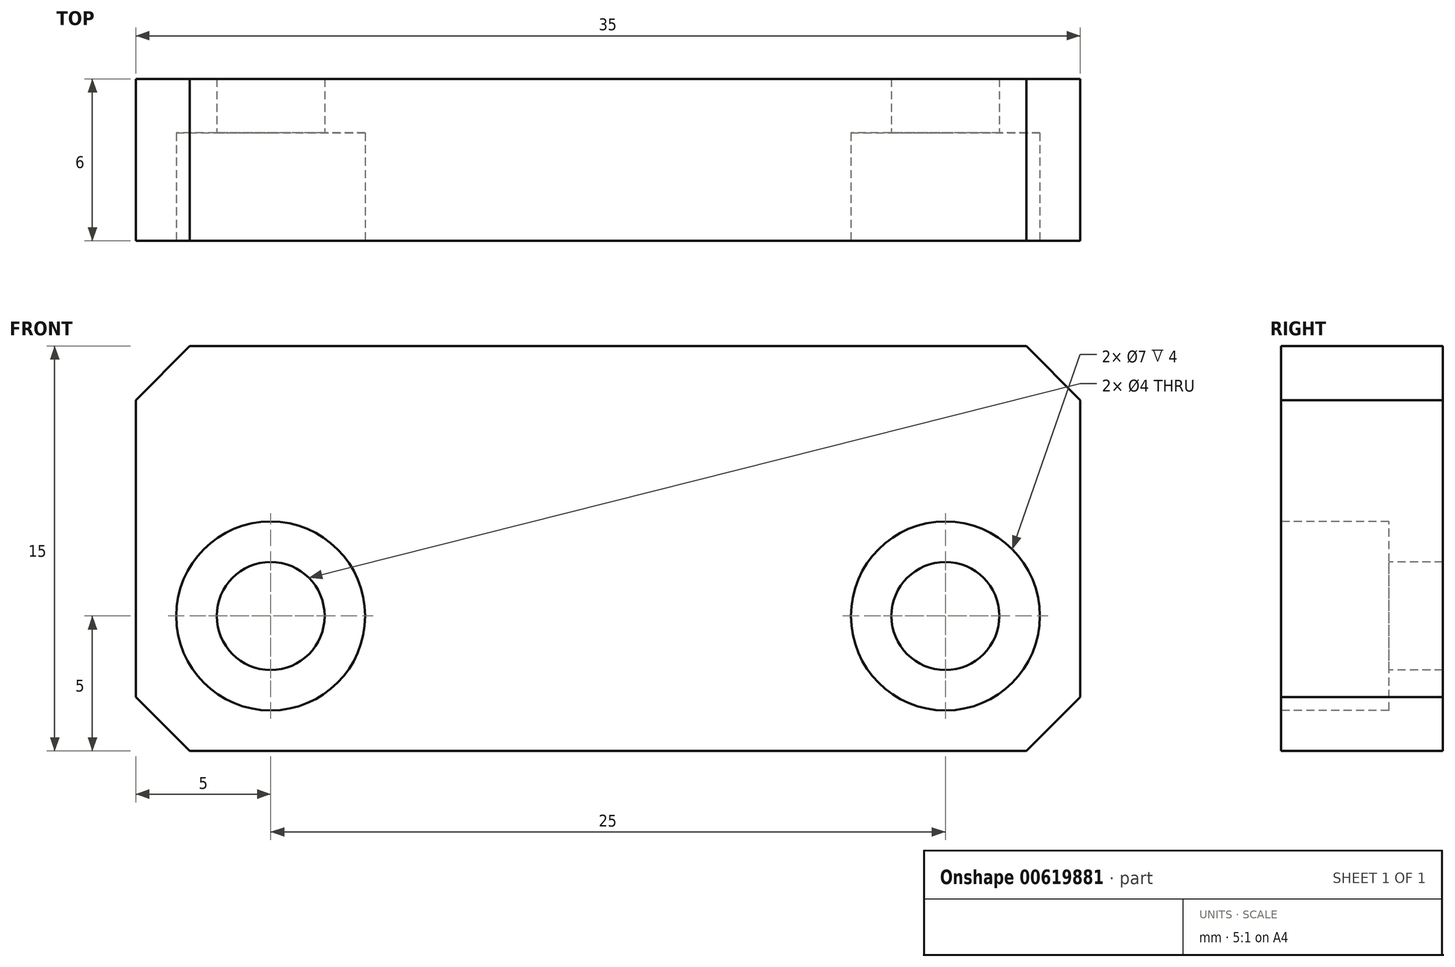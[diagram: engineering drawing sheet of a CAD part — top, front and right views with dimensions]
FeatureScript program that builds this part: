
annotation { "Feature Type Name" : "Feature", "Feature Type Description" : "" }
export const myFeature = defineFeature(function(context is Context, id is Id, definition is map)
    precondition{}
    {
        {
            var Q0;
            Q0=qCreatedBy(makeId("Front.planeOp"),FACE);
            var sketch = newSketch(context, id + "F0", { "sketchPlane" : qUnion([Q0])});
            skLineSegment(sketch, "E0.bottom", {"start": v(-17.5, 7.5) * mm, "end": v(17.5, 7.5) * mm});
            skLineSegment(sketch, "E0.top", {"start": v(-17.5, -7.5) * mm, "end": v(17.5, -7.5) * mm});
            skLineSegment(sketch, "E0.left", {"start": v(-17.5, 7.5) * mm, "end": v(-17.5, -7.5) * mm});
            skLineSegment(sketch, "E0.right", {"start": v(17.5, 7.5) * mm, "end": v(17.5, -7.5) * mm});
            skPoint(sketch, "E0.middle", {"position": v(0, 0) * mm});
            skSolve(sketch);
        }
        {
            var Q0;
            Q0=makeQuery(id+"F0.imprint","IMPRINT",FACE,{"disambiguationData":[TD([[makeQuery(id+"F0.imprint","IMPRINT",EDGE,{"derivedFrom":sQuery(id+"F0.wireOp",EDGE,"E0.bottom")}),-1.0]])]});
            extrude(context, id + "F1", {"entities" : qUnion([Q0]), "depth" : 6 * mm, "offsetDistance" : 25 * mm});
        }
        {
            var Q0;
            Q0=makeQuery(id+"F1.opExtrude","CAP_FACE",FACE,{"disambiguationData":[OSD([sQuery(id+"F0.wireOp",EDGE,"E0.bottom"),sQuery(id+"F0.wireOp",EDGE,"E0.top"),sQuery(id+"F0.wireOp",EDGE,"E0.left"),sQuery(id+"F0.wireOp",EDGE,"E0.right")])],"isStart":false});
            var sketch = newSketch(context, id + "F2", { "sketchPlane" : qUnion([Q0])});
            skCircle(sketch, "E1", {"center": v(12.5, -2.5) * mm, "radius": 3.5 * mm});
            skCircle(sketch, "E2.MirrorC", {"center": v(-12.5, -2.5) * mm, "radius": 3.5 * mm});
            skSolve(sketch);
        }
        {
            var Q0;
            Q0=qSketchRegion(id+"F2",true);
            extrude(context, id + "F3", {"entities" : qUnion([Q0]), "operationType" : NewBodyOperationType.REMOVE, "oppositeDirection" : true, "depth" : 4 * mm, "offsetDistance" : 25 * mm});
        }
        {
            var Q0;
            Q0=makeQuery(id+"F1.opExtrude","CAP_FACE",FACE,{"disambiguationData":[OSD([sQuery(id+"F0.wireOp",EDGE,"E0.bottom"),sQuery(id+"F0.wireOp",EDGE,"E0.top"),sQuery(id+"F0.wireOp",EDGE,"E0.left"),sQuery(id+"F0.wireOp",EDGE,"E0.right")])],"isStart":false});
            var sketch = newSketch(context, id + "F4", { "sketchPlane" : qUnion([Q0])});
            skPoint(sketch, "E3", {"position": v(12.5, -2.5) * mm});
            skPoint(sketch, "E4", {"position": v(-12.5, -2.5) * mm});
            skCircle(sketch, "E5", {"center": v(12.5, -2.5) * mm, "radius": 2 * mm});
            skCircle(sketch, "E6", {"center": v(-12.5, -2.5) * mm, "radius": 2 * mm});
            skSolve(sketch);
        }
        {
            var Q0;
            Q0=qSketchRegion(id+"F4",true);
            extrude(context, id + "F5", {"entities" : qUnion([Q0]), "operationType" : NewBodyOperationType.REMOVE, "endBound" : BoundingType.THROUGH_ALL, "oppositeDirection" : true, "depth" : 25 * mm, "offsetDistance" : 25 * mm});
        }
        {
            var Q0;
            Q0=makeQuery(id+"F1.opExtrude","SWEPT_EDGE",EDGE,{"disambiguationData":[OSD([sQuery(id+"F0.wireOp",EDGE,"E0.bottom"),sQuery(id+"F0.wireOp",EDGE,"E0.left")])]});
            var Q1;
            Q1=makeQuery(id+"F1.opExtrude","SWEPT_EDGE",EDGE,{"disambiguationData":[OSD([sQuery(id+"F0.wireOp",EDGE,"E0.bottom"),sQuery(id+"F0.wireOp",EDGE,"E0.right")])]});
            var Q2;
            Q2=makeQuery(id+"F1.opExtrude","SWEPT_EDGE",EDGE,{"disambiguationData":[OSD([sQuery(id+"F0.wireOp",EDGE,"E0.top"),sQuery(id+"F0.wireOp",EDGE,"E0.right")])]});
            var Q3;
            Q3=makeQuery(id+"F1.opExtrude","SWEPT_EDGE",EDGE,{"disambiguationData":[OSD([sQuery(id+"F0.wireOp",EDGE,"E0.top"),sQuery(id+"F0.wireOp",EDGE,"E0.left")])]});
            chamfer(context, id + "F6", {"entities" : qUnion([Q0, Q1, Q2, Q3]), "width" : 2 * mm, "tangentPropagation" : true});
        }
    });
